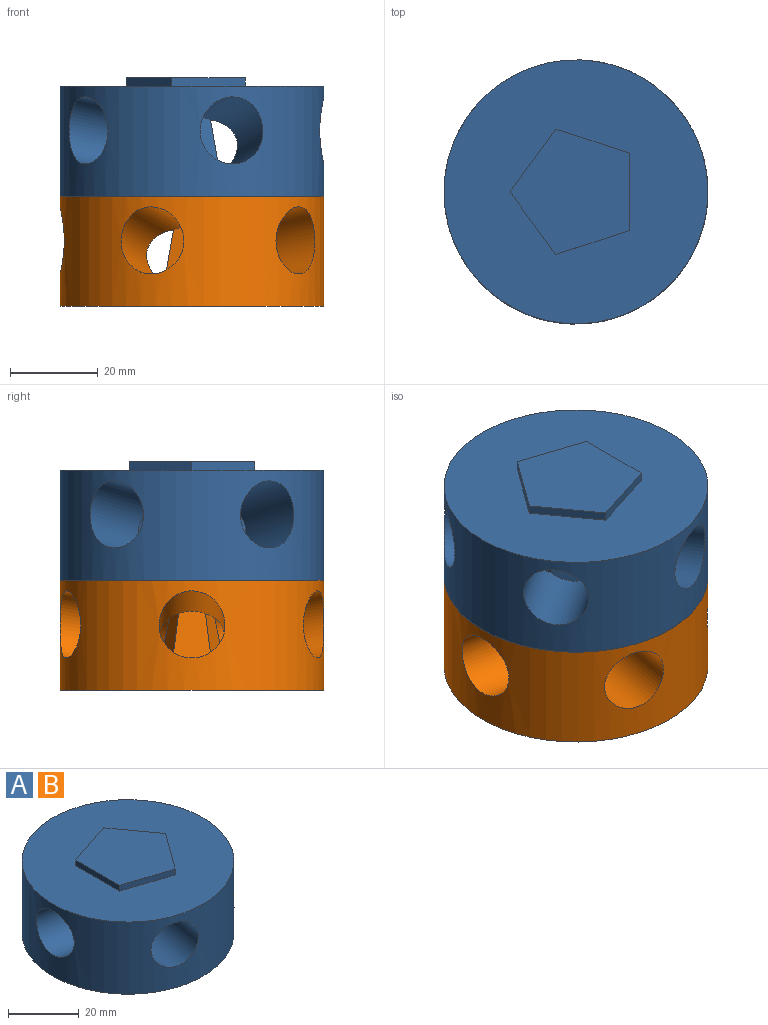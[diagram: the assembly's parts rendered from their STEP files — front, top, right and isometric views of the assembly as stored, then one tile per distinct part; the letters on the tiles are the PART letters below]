
ASSEMBLY  parts=2 mates=1
PART A: 25 faces, bbox 62.6x64.8x27 mm
  f0: plane 60x60mm, normal (0,0,-1), area 2218.8mm2, adj f1,f19,f20,f21,f22,f23
  f1: cylinder r=30mm len=60mm, axis (0,0,-1), area 3808.2mm2, adj f0,f2,f3,f6,f8,f10,f12
  f2: plane 60x60mm, normal (0,0,1), area 2292.5mm2, adj f1,f13,f14,f15,f16,f17
  f3: cylinder r=7.5mm len=28.53mm, axis (0.98,0,-0.17), area 1052.5mm2, adj f1,f4,f6,f12
  f4: plane 14.77x9.3mm, normal (-0.98,0,0.17), area 110.9mm2, adj f3,f5,f11
  f5: plane 14.77x8.85mm, normal (-0.3,-0.94,0.17), area 110.9mm2, adj f4,f6,f7
  f6: cylinder r=7.5mm len=29.91mm, axis (0.3,0.94,-0.17), area 1052.5mm2, adj f1,f3,f5,f8
  f7: plane 14.77x7.53mm, normal (0.8,-0.58,0.17), area 110.9mm2, adj f5,f8,f9
  f8: cylinder r=7.5mm len=30.04mm, axis (-0.8,0.58,-0.17), area 1052.5mm2, adj f1,f6,f7,f10
  f9: plane 14.77x7.53mm, normal (0.8,0.58,0.17), area 110.9mm2, adj f7,f10,f11
  f10: cylinder r=7.5mm len=30.04mm, axis (-0.8,-0.58,-0.17), area 1052.5mm2, adj f1,f8,f9,f12
  f11: plane 14.77x8.85mm, normal (-0.3,0.94,0.17), area 110.9mm2, adj f4,f9,f12
  f12: cylinder r=7.5mm len=29.91mm, axis (0.3,-0.94,-0.17), area 1052.5mm2, adj f1,f3,f10,f11
  f13: plane 16.77x5.45mm, normal (-0.31,0.95,0), area 35.3mm2, adj f2,f14,f17,f18
  f14: plane 17.63x2mm, normal (-1,0,0), area 35.3mm2, adj f2,f13,f15,f18
  f15: plane 16.77x5.45mm, normal (-0.31,-0.95,0), area 35.3mm2, adj f2,f14,f16,f18
  f16: plane 14.27x10.36mm, normal (0.81,-0.59,0), area 35.3mm2, adj f2,f15,f17,f18
  f17: plane 14.27x10.36mm, normal (0.81,0.59,0), area 35.3mm2, adj f2,f13,f16,f18
  f18: plane 28.53x27.14mm, normal (0,0,1), area 535mm2, adj f13,f14,f15,f16,f17
  f19: plane 18.81x2mm, normal (-1,0,0), area 37.6mm2, adj f0,f20,f23,f24
  f20: plane 17.89x5.81mm, normal (-0.31,0.95,0), area 37.6mm2, adj f0,f19,f21,f24
  f21: plane 15.22x11.06mm, normal (0.81,0.59,0), area 37.6mm2, adj f0,f20,f22,f24
  f22: plane 15.22x11.06mm, normal (0.81,-0.59,0), area 37.6mm2, adj f0,f21,f23,f24
  f23: plane 17.89x5.81mm, normal (-0.31,-0.95,0), area 37.6mm2, adj f0,f19,f22,f24
  f24: plane 30.43x28.94mm, normal (0,0,-1), area 608.7mm2, adj f19,f20,f21,f22,f23
PART B: same geometry as A
PLACE A rot(axis=(0,0,1),180deg) t=(-32.49,-44.69,17.41)mm
PLACE B t=(-32.49,-44.69,-7.59)mm
MATE fastened A.f1 <-> B.f1  axis (0,0,-1) through (-32.49,-44.69,19.41)mm
